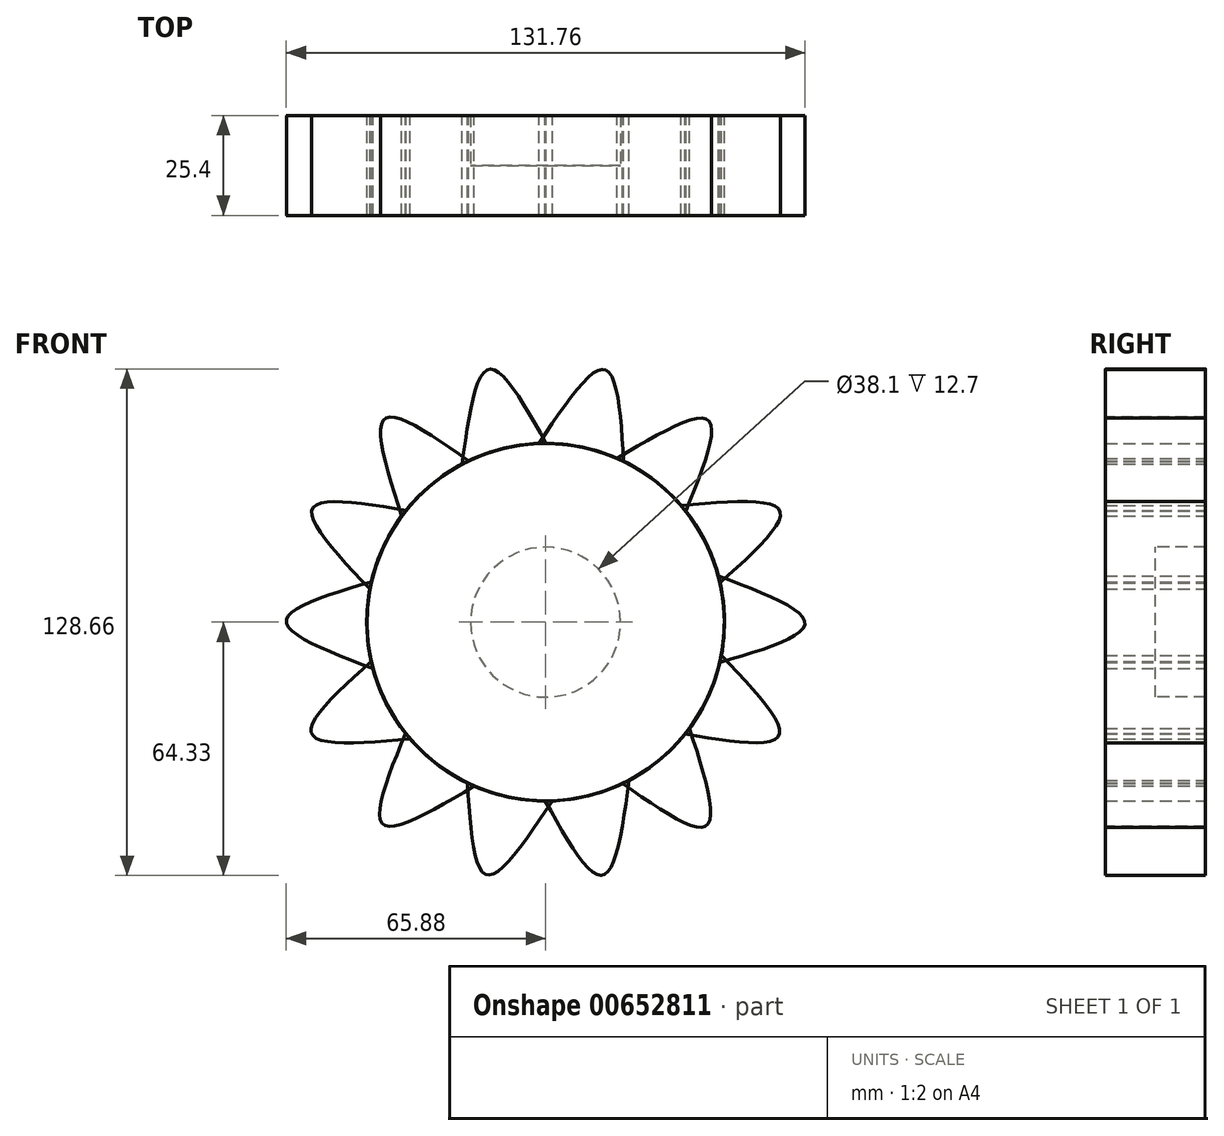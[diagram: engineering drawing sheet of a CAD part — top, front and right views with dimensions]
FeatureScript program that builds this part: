
annotation { "Feature Type Name" : "Feature", "Feature Type Description" : "" }
export const myFeature = defineFeature(function(context is Context, id is Id, definition is map)
    precondition{}
    {
        {
            var Q0;
            Q0=qCreatedBy(makeId("Front.planeOp"),FACE);
            var sketch = newSketch(context, id + "F0", { "sketchPlane" : qUnion([Q0])});
            skCircle(sketch, "E0", {"center": v(0, 0) * mm, "radius": 45.43 * mm});
            skFitSpline(sketch, "E1", {"points": [v(-36.56, 26.96) * mm, v(-40.82, 51.7) * mm, v(-19.6, 40.98) * mm], "startDerivative": vector(-21.52, 66.77) * mm, "endDerivative": vector(55.77, -39.2) * mm});
            skSolve(sketch);
        }
        {
            var Q0;
            Q0 = qSketchRegion(id + "F0", true);
            extrude(context, id + "F1", {"entities" : qUnion([Q0]), "endBound" : BoundingType.SYMMETRIC, "depth" : 25.4 * mm, "offsetDistance" : 25.4 * mm});
        }
        {
            var Q0;
            Q0=makeQuery(id+"F1.opExtrude","SWEPT_BODY",BODY,{"disambiguationData":[OSD([sQuery(id+"F0.wireOp",EDGE,"E0"),sQuery(id+"F0.wireOp",EDGE,"E1")])]});
            var Q1;
            Q1=makeQuery(id+"F1.opExtrude","CAP_EDGE",EDGE,{"disambiguationData":[OSD([sQuery(id+"F0.wireOp",EDGE,"E0")])],"isStart":false});
            circularPattern(context, id + "F2", {"entities" : qUnion([Q0]), "axis" : qUnion([Q1]), "angle" : 360 * degree, "instanceCount" : 14, "equalSpace" : true});
        }
        {
            var Q0;
            Q0=qCreatedBy(makeId("Front.planeOp"),FACE);
            var sketch = newSketch(context, id + "F3", { "sketchPlane" : qUnion([Q0])});
            skCircle(sketch, "E2", {"center": v(0, 0) * mm, "radius": 25.92 * mm});
            skSolve(sketch);
        }
        {
            var Q0;
            Q0=sQuery(id+"F3.wireOp",VERTEX,"E2.center");
            var Q1;
            Q1=makeQuery(id+"F2.opPattern","COPY",BODY,{"derivedFrom":makeQuery(id+"F1.opExtrude","SWEPT_BODY",BODY,{"disambiguationData":[OSD([sQuery(id+"F0.wireOp",EDGE,"E0"),sQuery(id+"F0.wireOp",EDGE,"E1")])]}),"instanceName":"10"});
            hole(context, id + "F4", {"style" : HoleStyle.SIMPLE, "endStyle" : HoleEndStyle.THROUGH, "holeDiameter" : 38.1 * mm, "majorDiameter" : 6.35 * mm, "isTappedThrough" : true, "tappedDepth" : 12.7 * mm, "tapClearance" : 3, "locations" : qUnion([Q0]), "scope" : qUnion([Q1])});
        }
    });
